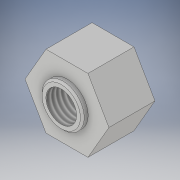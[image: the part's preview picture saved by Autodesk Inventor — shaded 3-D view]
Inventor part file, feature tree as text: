
AUTODESK INVENTOR PART (.ipt)
format: ipt  version: 2017 (Build 210142000, 142)  size: 135,680 bytes
history: native  units: mm
features: other x2, extrude x2, chamfer x2, sketch x2, mirror x1, thread x1
ambient origin geometry x8: Origin, YZ Plane, XZ Plane, XY Plane, X Axis, Y Axis, Z Axis, Center Point
bodies: Body1 (feature_tree)
feature tree (10):
  other  "Твердое тело1"
  extrude  "Выдавливание1"  Depth=12.0mm TaperAngle=0.0deg
  extrude  "Выдавливание3"  Depth=8.0mm
  chamfer  "Фаска2"  Angle=120.0deg  [1 undecoded]
  other  "РабПлоскость1"
  mirror  "Зеркальное отражение1"
  chamfer  "Фаска3"  Angle=120.0deg  [1 undecoded]
  thread  "Резьба1"
  sketch  "Эскиз1"
  sketch  "Эскиз3"
note: 2 required parameter values undecoded (feature->parameter linkage not recoverable at this tier; creation-order binding heuristic only, values carry confidence <= 0.55)
